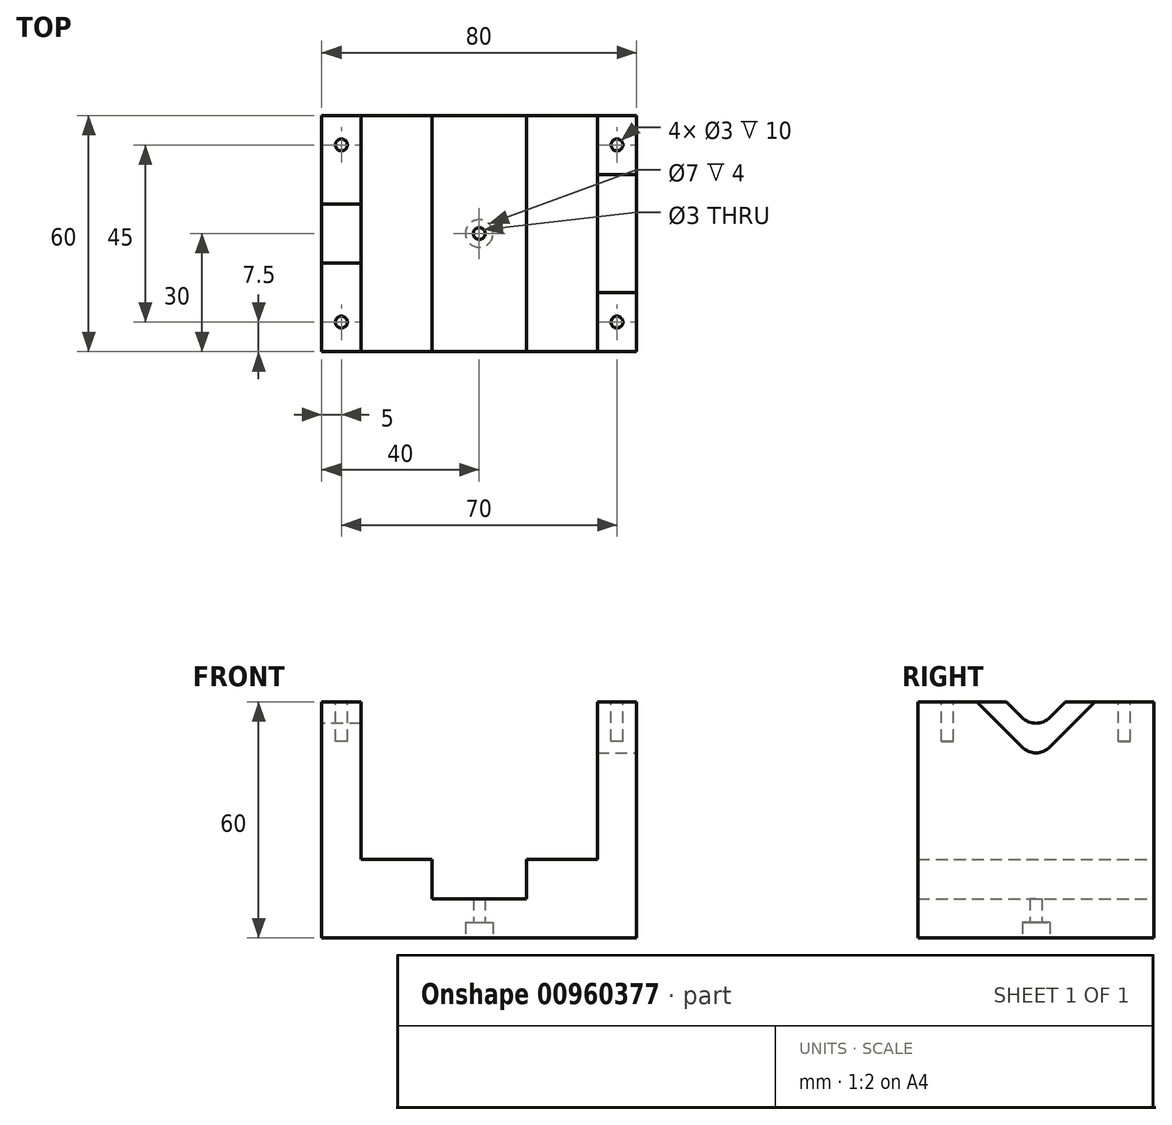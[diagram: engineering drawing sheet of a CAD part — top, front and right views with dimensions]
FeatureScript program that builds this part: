
annotation { "Feature Type Name" : "Feature", "Feature Type Description" : "" }
export const myFeature = defineFeature(function(context is Context, id is Id, definition is map)
    precondition{}
    {
        {
            var Q0;
            Q0=qCreatedBy(makeId("Front.planeOp"),FACE);
            var sketch = newSketch(context, id + "F0", { "sketchPlane" : qUnion([Q0])});
            skLineSegment(sketch, "E0.bottom", {"start": v(-40, 0) * mm, "end": v(40, 0) * mm});
            skLineSegment(sketch, "E0.left", {"start": v(-40, 0) * mm, "end": v(-40, 60) * mm});
            skLineSegment(sketch, "E0.right", {"start": v(40, 0) * mm, "end": v(40, 60) * mm});
            skLineSegment(sketch, "E1", {"start": v(-40, 60) * mm, "end": v(-30, 60) * mm});
            skLineSegment(sketch, "E2", {"start": v(-30, 60) * mm, "end": v(-30, 20) * mm});
            skLineSegment(sketch, "E3", {"start": v(-30, 20) * mm, "end": v(-12, 20) * mm});
            skLineSegment(sketch, "E4", {"start": v(-12, 20) * mm, "end": v(-12, 10) * mm});
            skLineSegment(sketch, "E5", {"start": v(-12, 10) * mm, "end": v(12, 10) * mm});
            skLineSegment(sketch, "E6", {"start": v(12, 10) * mm, "end": v(12, 20) * mm});
            skLineSegment(sketch, "E7", {"start": v(12, 20) * mm, "end": v(30, 20) * mm});
            skLineSegment(sketch, "E8", {"start": v(30, 20) * mm, "end": v(30, 60) * mm});
            skLineSegment(sketch, "E9", {"start": v(30, 60) * mm, "end": v(40, 60) * mm});
            skSolve(sketch);
        }
        {
            var Q0;
            Q0 = qSketchRegion(id + "F0", true);
            extrude(context, id + "F1", {"entities" : qUnion([Q0]), "depth" : 60 * mm, "offsetDistance" : 25 * mm});
        }
        {
            var Q0;
            Q0=makeQuery(id+"F1.opExtrude","SWEPT_FACE",FACE,{"disambiguationData":[OSD([sQuery(id+"F0.wireOp",EDGE,"E0.right")])]});
            var sketch = newSketch(context, id + "F2", { "sketchPlane" : qUnion([Q0])});
            skLineSegment(sketch, "E10", {"start": v(-26.46, 48.54) * mm, "end": v(-15, 60) * mm});
            skLineSegment(sketch, "E11", {"start": v(-33.54, 48.54) * mm, "end": v(-45, 60) * mm});
            skPoint(sketch, "E12.visualSharp", {"position": v(-30, 45) * mm});
            skArc(sketch, "E12.filletArc", {"start": v(-33.54, 48.54) * mm, "mid": v(-30, 47.07) * mm, "end": v(-26.46, 48.54) * mm});
            skSolve(sketch);
        }
        {
            var Q0;
            {var subQ0=sQuery(id+"F2.wireOp",EDGE,"E10");Q0=makeQuery(id+"F2.imprint","IMPRINT",FACE,{"disambiguationData":[TD([[makeQuery(id+"F2.imprint","IMPRINT",EDGE,{"derivedFrom":subQ0}),1.0]])]});}
            extrude(context, id + "F3", {"entities" : qUnion([Q0]), "operationType" : NewBodyOperationType.REMOVE, "endBound" : BoundingType.UP_TO_NEXT, "oppositeDirection" : true, "depth" : 25 * mm, "offsetDistance" : 25 * mm});
        }
        {
            var Q0;
            Q0=makeQuery(id+"F1.opExtrude","SWEPT_FACE",FACE,{"disambiguationData":[OSD([sQuery(id+"F0.wireOp",EDGE,"E0.left")])]});
            var sketch = newSketch(context, id + "F4", { "sketchPlane" : qUnion([Q0])});
            skLineSegment(sketch, "E13", {"start": v(22.5, 60) * mm, "end": v(26.46, 56.04) * mm});
            skPoint(sketch, "E13.endSnap0", {"position": v(30, 60) * mm});
            skLineSegment(sketch, "E14", {"start": v(33.54, 56.04) * mm, "end": v(37.5, 60) * mm});
            skPoint(sketch, "E15.visualSharp", {"position": v(30, 52.5) * mm});
            skArc(sketch, "E15.filletArc", {"start": v(26.46, 56.04) * mm, "mid": v(30, 54.57) * mm, "end": v(33.54, 56.04) * mm});
            skSolve(sketch);
        }
        {
            var Q0;
            {var subQ0=sQuery(id+"F4.wireOp",EDGE,"E13");Q0=makeQuery(id+"F4.imprint","IMPRINT",FACE,{"disambiguationData":[TD([[makeQuery(id+"F4.imprint","IMPRINT",EDGE,{"derivedFrom":subQ0}),1.0]])]});}
            extrude(context, id + "F5", {"entities" : qUnion([Q0]), "operationType" : NewBodyOperationType.REMOVE, "endBound" : BoundingType.UP_TO_NEXT, "oppositeDirection" : true, "depth" : 25 * mm, "offsetDistance" : 25 * mm});
        }
        {
            var Q0;
            {var subQ1=sQuery(id+"F0.wireOp",EDGE,"E1");Q0=makeQuery(id+"F5.boolean.opBoolean","SPLIT",FACE,{"disambiguationData":[TD([makeQuery(id+"F5.opExtrude","SWEPT_FACE",FACE,{"disambiguationData":[OSD([sQuery(id+"F4.wireOp",EDGE,"E13")])]})])],"derivedFrom":makeQuery(id+"F1.opExtrude","SWEPT_FACE",FACE,{"disambiguationData":[OSD([subQ1])]})});}
            var sketch = newSketch(context, id + "F6", { "sketchPlane" : qUnion([Q0])});
            skCircle(sketch, "E16", {"center": v(-35, -7.5) * mm, "radius": 1.5 * mm});
            skPoint(sketch, "E16.centerSnap0", {"position": v(-30, -11.25) * mm});
            skPoint(sketch, "E16.centerSnap1", {"position": v(-35, 0) * mm});
            skSolve(sketch);
        }
        {
            var Q0;
            {var subQ1=sQuery(id+"F0.wireOp",EDGE,"E1");Q0=makeQuery(id+"F5.boolean.opBoolean","SPLIT",FACE,{"disambiguationData":[TD([makeQuery(id+"F5.opExtrude","SWEPT_FACE",FACE,{"disambiguationData":[OSD([sQuery(id+"F4.wireOp",EDGE,"E14")])]})])],"derivedFrom":makeQuery(id+"F1.opExtrude","SWEPT_FACE",FACE,{"disambiguationData":[OSD([subQ1])]})});}
            var sketch = newSketch(context, id + "F7", { "sketchPlane" : qUnion([Q0])});
            skCircle(sketch, "E17", {"center": v(-35, -52.5) * mm, "radius": 1.5 * mm});
            skPoint(sketch, "E17.centerSnap0", {"position": v(-35, -60) * mm});
            skPoint(sketch, "E17.centerSnap1", {"position": v(-40, -48.75) * mm});
            skSolve(sketch);
        }
        {
            var Q0;
            {var subQ0=sQuery(id+"F0.wireOp",EDGE,"E9");Q0=makeQuery(id+"F3.boolean.opBoolean","SPLIT",FACE,{"disambiguationData":[TD([makeQuery(id+"F3.opExtrude","SWEPT_FACE",FACE,{"disambiguationData":[OSD([sQuery(id+"F2.wireOp",EDGE,"E10")])]})])],"derivedFrom":makeQuery(id+"F1.opExtrude","SWEPT_FACE",FACE,{"disambiguationData":[OSD([subQ0])]})});}
            var sketch = newSketch(context, id + "F8", { "sketchPlane" : qUnion([Q0])});
            skCircle(sketch, "E18", {"center": v(35, -7.5) * mm, "radius": 1.5 * mm});
            skPoint(sketch, "E18.centerSnap0", {"position": v(40, -7.5) * mm});
            skPoint(sketch, "E18.centerSnap1", {"position": v(35, 0) * mm});
            skSolve(sketch);
        }
        {
            var Q0;
            {var subQ0=sQuery(id+"F0.wireOp",EDGE,"E9");Q0=makeQuery(id+"F3.boolean.opBoolean","SPLIT",FACE,{"disambiguationData":[TD([makeQuery(id+"F3.opExtrude","SWEPT_FACE",FACE,{"disambiguationData":[OSD([sQuery(id+"F2.wireOp",EDGE,"E11")])]})])],"derivedFrom":makeQuery(id+"F1.opExtrude","SWEPT_FACE",FACE,{"disambiguationData":[OSD([subQ0])]})});}
            var sketch = newSketch(context, id + "F9", { "sketchPlane" : qUnion([Q0])});
            skPoint(sketch, "E19.centerSnap0", {"position": v(40, -52.5) * mm});
            skCircle(sketch, "E20", {"center": v(35, -52.5) * mm, "radius": 1.5 * mm});
            skPoint(sketch, "E20.centerSnap0", {"position": v(35, -60) * mm});
            skSolve(sketch);
        }
        {
            var Q0;
            Q0 = qSketchRegion(id + "F6", true);
            var Q1;
            Q1 = qSketchRegion(id + "F7", true);
            var Q2;
            Q2 = qSketchRegion(id + "F8", true);
            var Q3;
            Q3 = qSketchRegion(id + "F9", true);
            extrude(context, id + "F10", {"entities" : qUnion([Q0, Q1, Q2, Q3]), "operationType" : NewBodyOperationType.REMOVE, "oppositeDirection" : true, "depth" : 10 * mm, "offsetDistance" : 25 * mm});
        }
        {
            var Q0;
            Q0=makeQuery(id+"F1.opExtrude","SWEPT_FACE",FACE,{"disambiguationData":[OSD([sQuery(id+"F0.wireOp",EDGE,"E0.bottom")])]});
            var sketch = newSketch(context, id + "F11", { "sketchPlane" : qUnion([Q0])});
            skCircle(sketch, "E21", {"center": v(0, 30) * mm, "radius": 3.5 * mm});
            skSolve(sketch);
        }
        {
            var Q0;
            Q0=makeQuery(id+"F11.imprint","IMPRINT",FACE,{"disambiguationData":[TD([[makeQuery(id+"F11.imprint","IMPRINT",EDGE,{"derivedFrom":sQuery(id+"F11.wireOp",EDGE,"Yno15AQk-Opuc-OZcd-AXqb-1jMAF34N43zU")}),-1.0]])]});
            var Q1;
            Q1=makeQuery(id+"F11.imprint","IMPRINT",FACE,{"disambiguationData":[TD([[makeQuery(id+"F11.imprint","IMPRINT",EDGE,{"derivedFrom":sQuery(id+"F11.wireOp",EDGE,"E21")}),1.0]])]});
            var Q2;
            Q2=sQuery(id+"F11.wireOp",EDGE,"E21");
            extrude(context, id + "F12", {"entities" : qUnion([Q0, Q1]), "operationType" : NewBodyOperationType.REMOVE, "surfaceEntities" : qUnion([Q2]), "oppositeDirection" : true, "depth" : 4 * mm, "offsetDistance" : 25 * mm});
        }
        {
            var Q0;
            Q0=makeQuery(id+"F12.boolean.opBoolean","COPY",FACE,{"derivedFrom":makeQuery(id+"F12.opExtrude","CAP_FACE",FACE,{"disambiguationData":[OSD([sQuery(id+"F11.wireOp",EDGE,"E21")])],"isStart":false})});
            var sketch = newSketch(context, id + "F13", { "sketchPlane" : qUnion([Q0])});
            skCircle(sketch, "E22", {"center": v(0, 30) * mm, "radius": 1.5 * mm});
            skSolve(sketch);
        }
        {
            var Q0;
            Q0 = qSketchRegion(id + "F13", true);
            extrude(context, id + "F14", {"entities" : qUnion([Q0]), "operationType" : NewBodyOperationType.REMOVE, "endBound" : BoundingType.UP_TO_NEXT, "oppositeDirection" : true, "depth" : 25 * mm, "offsetDistance" : 25 * mm});
        }
    });
